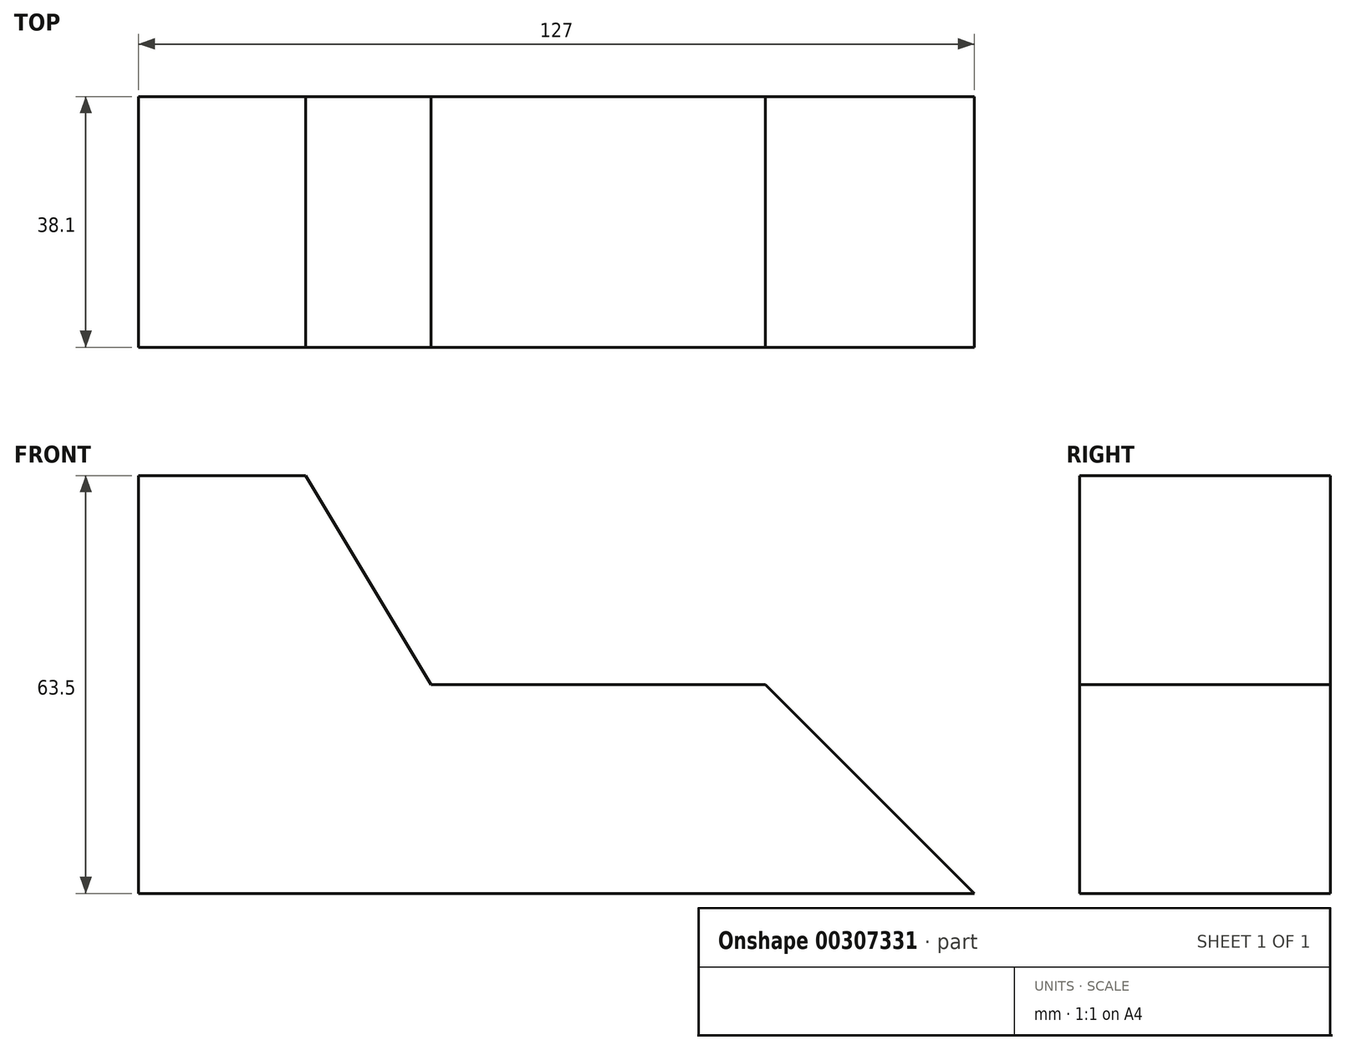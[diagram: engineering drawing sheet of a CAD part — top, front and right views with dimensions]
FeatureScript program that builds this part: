
annotation { "Feature Type Name" : "Feature", "Feature Type Description" : "" }
export const myFeature = defineFeature(function(context is Context, id is Id, definition is map)
    precondition{}
    {
        {
            var Q0;
            Q0=qCreatedBy(makeId("Front.planeOp"),FACE);
            var sketch = newSketch(context, id + "F0", { "sketchPlane" : qUnion([Q0])});
            skLineSegment(sketch, "E0", {"start": v(-55.59, -17.32) * mm, "end": v(71.41, -17.32) * mm});
            skLineSegment(sketch, "E1", {"start": v(-55.59, -17.32) * mm, "end": v(-55.59, 46.18) * mm});
            skLineSegment(sketch, "E2", {"start": v(-55.59, 46.18) * mm, "end": v(-30.19, 46.18) * mm});
            skLineSegment(sketch, "E3", {"start": v(39.66, 14.43) * mm, "end": v(-11.14, 14.43) * mm});
            skLineSegment(sketch, "E4", {"start": v(-11.14, 14.43) * mm, "end": v(-30.19, 46.18) * mm});
            skLineSegment(sketch, "E5", {"start": v(39.66, 14.43) * mm, "end": v(71.41, -17.32) * mm});
            skSolve(sketch);
        }
        {
            var Q0;
            Q0=makeQuery(id+"F0.imprint","IMPRINT",FACE,{"disambiguationData":[TD([[makeQuery(id+"F0.imprint","IMPRINT",EDGE,{"derivedFrom":sQuery(id+"F0.wireOp",EDGE,"E0")}),1.0]])]});
            extrude(context, id + "F1", {"entities" : qUnion([Q0]), "depth" : 38.1 * mm});
        }
    });
